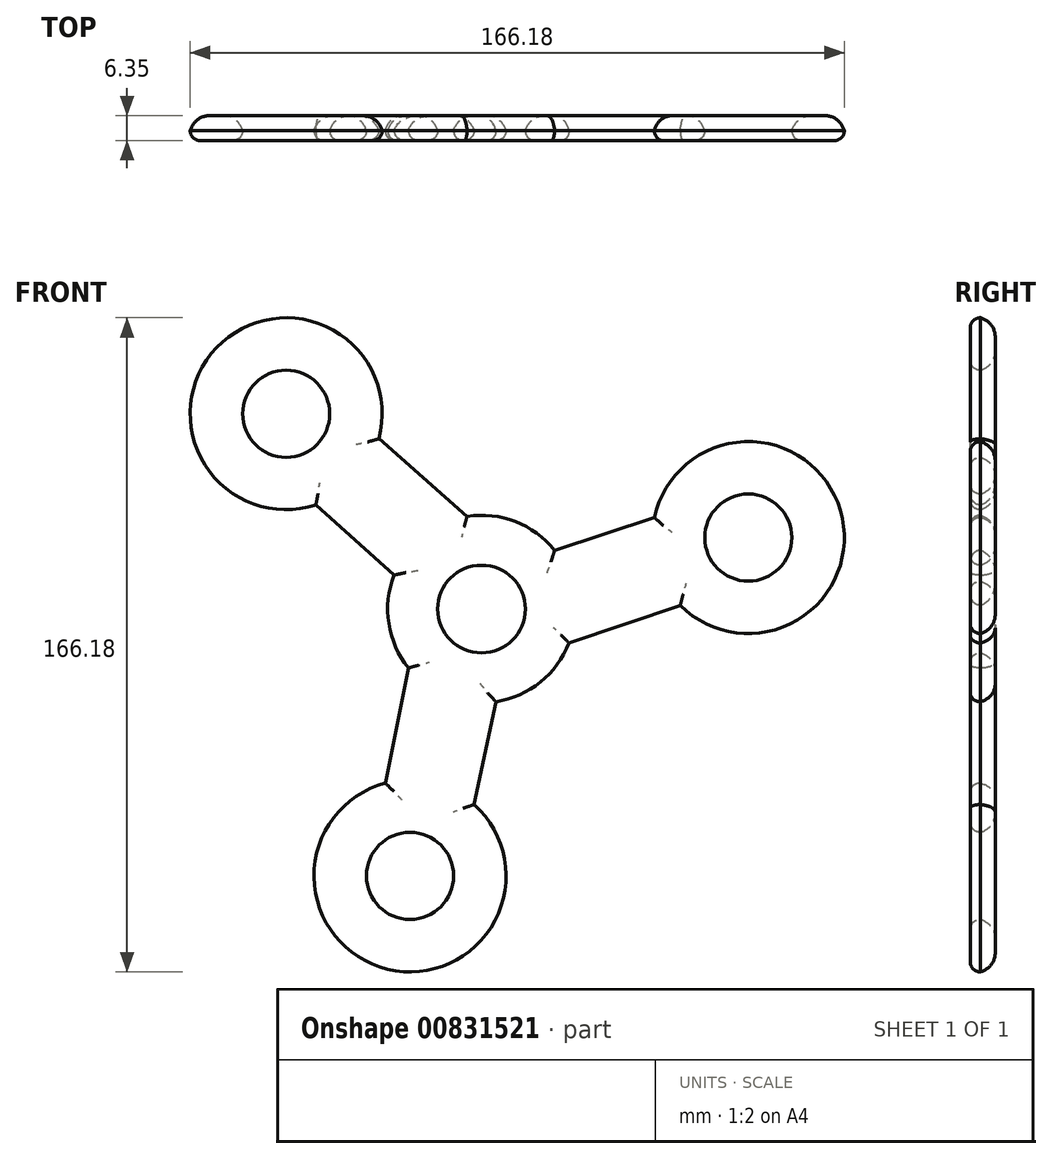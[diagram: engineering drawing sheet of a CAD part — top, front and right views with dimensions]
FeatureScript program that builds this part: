
annotation { "Feature Type Name" : "Feature", "Feature Type Description" : "" }
export const myFeature = defineFeature(function(context is Context, id is Id, definition is map)
    precondition{}
    {
        {
            var Q0;
            Q0=qCreatedBy(makeId("Front.planeOp"),FACE);
            var sketch = newSketch(context, id + "F0", { "sketchPlane" : qUnion([Q0])});
            skCircle(sketch, "E0", {"center": v(-49.62, 49.62) * mm, "radius": 11.07 * mm});
            skArc(sketch, "E1", {"start": v(-26.08, 43.27) * mm, "mid": v(-67.3, 66.43) * mm, "end": v(-42.1, 26.43) * mm});
            skCircle(sketch, "E2", {"center": v(0, 0) * mm, "radius": 11.13 * mm});
            skArc(sketch, "E3", {"start": v(-22.22, 8.61) * mm, "mid": v(-23.55, -3.66) * mm, "end": v(-18.57, -14.94) * mm});
            skLineSegment(sketch, "E4", {"start": v(-42.1, 26.43) * mm, "end": v(-22.22, 8.61) * mm});
            skLineSegment(sketch, "E5", {"start": v(-26.08, 43.27) * mm, "end": v(-3.66, 23.55) * mm});
            skCircle(sketch, "E6.1.0", {"center": v(-18.16, -67.79) * mm, "radius": 11.07 * mm});
            skArc(sketch, "E6.1.1", {"start": v(-24.43, -44.22) * mm, "mid": v(-23.88, -91.5) * mm, "end": v(-1.85, -49.67) * mm});
            skLineSegment(sketch, "E6.1.2", {"start": v(-1.85, -49.67) * mm, "end": v(3.65, -23.55) * mm});
            skLineSegment(sketch, "E6.1.3", {"start": v(-24.43, -44.22) * mm, "end": v(-18.57, -14.94) * mm});
            skCircle(sketch, "E6.2.0", {"center": v(67.79, 18.16) * mm, "radius": 11.07 * mm});
            skArc(sketch, "E6.2.1", {"start": v(50.52, 0.95) * mm, "mid": v(91.18, 25.07) * mm, "end": v(43.94, 23.24) * mm});
            skLineSegment(sketch, "E6.2.2", {"start": v(43.94, 23.24) * mm, "end": v(18.57, 14.94) * mm});
            skLineSegment(sketch, "E6.2.3", {"start": v(50.52, 0.95) * mm, "end": v(22.22, -8.6) * mm});
            skArc(sketch, "E7.trimOffspring", {"start": v(18.57, 14.94) * mm, "mid": v(8.6, 22.22) * mm, "end": v(-3.66, 23.55) * mm});
            skArc(sketch, "E8.trimOffspring", {"start": v(3.65, -23.55) * mm, "mid": v(14.94, -18.57) * mm, "end": v(22.22, -8.6) * mm});
            skSolve(sketch);
        }
        {
            var Q0;
            Q0 = qSketchRegion(id + "F0", true);
            extrude(context, id + "F1", {"entities" : qUnion([Q0]), "depth" : 6.35 * mm, "offsetDistance" : 25.4 * mm});
        }
        {
            var Q0;
            Q0=makeQuery(id+"F1.opExtrude","CAP_FACE",FACE,{"disambiguationData":[OSD([sQuery(id+"F0.wireOp",EDGE,"E0"),sQuery(id+"F0.wireOp",EDGE,"E1"),sQuery(id+"F0.wireOp",EDGE,"E2"),sQuery(id+"F0.wireOp",EDGE,"E3"),sQuery(id+"F0.wireOp",EDGE,"E4"),sQuery(id+"F0.wireOp",EDGE,"E5"),sQuery(id+"F0.wireOp",EDGE,"E6.1.0"),sQuery(id+"F0.wireOp",EDGE,"E6.1.1"),sQuery(id+"F0.wireOp",EDGE,"E6.1.2"),sQuery(id+"F0.wireOp",EDGE,"E6.1.3"),sQuery(id+"F0.wireOp",EDGE,"E6.2.0"),sQuery(id+"F0.wireOp",EDGE,"E6.2.1"),sQuery(id+"F0.wireOp",EDGE,"E6.2.2"),sQuery(id+"F0.wireOp",EDGE,"E6.2.3"),sQuery(id+"F0.wireOp",EDGE,"E7.trimOffspring"),sQuery(id+"F0.wireOp",EDGE,"E8.trimOffspring")])],"isStart":false});
            fillet(context, id + "F2", {"entities" : qUnion([Q0]), "radius" : 2.54 * mm, "tangentPropagation" : true, "allowEdgeOverflow" : false});
        }
        {
            var Q0;
            Q0=makeQuery(id+"F1.opExtrude","CAP_FACE",FACE,{"disambiguationData":[OSD([sQuery(id+"F0.wireOp",EDGE,"E0"),sQuery(id+"F0.wireOp",EDGE,"E1"),sQuery(id+"F0.wireOp",EDGE,"E2"),sQuery(id+"F0.wireOp",EDGE,"E3"),sQuery(id+"F0.wireOp",EDGE,"E4"),sQuery(id+"F0.wireOp",EDGE,"E5"),sQuery(id+"F0.wireOp",EDGE,"E6.1.0"),sQuery(id+"F0.wireOp",EDGE,"E6.1.1"),sQuery(id+"F0.wireOp",EDGE,"E6.1.2"),sQuery(id+"F0.wireOp",EDGE,"E6.1.3"),sQuery(id+"F0.wireOp",EDGE,"E6.2.0"),sQuery(id+"F0.wireOp",EDGE,"E6.2.1"),sQuery(id+"F0.wireOp",EDGE,"E6.2.2"),sQuery(id+"F0.wireOp",EDGE,"E6.2.3"),sQuery(id+"F0.wireOp",EDGE,"E7.trimOffspring"),sQuery(id+"F0.wireOp",EDGE,"E8.trimOffspring")])],"isStart":true});
            fillet(context, id + "F3", {"entities" : qUnion([Q0]), "radius" : 5.08 * mm, "tangentPropagation" : true, "allowEdgeOverflow" : false});
        }
    });
